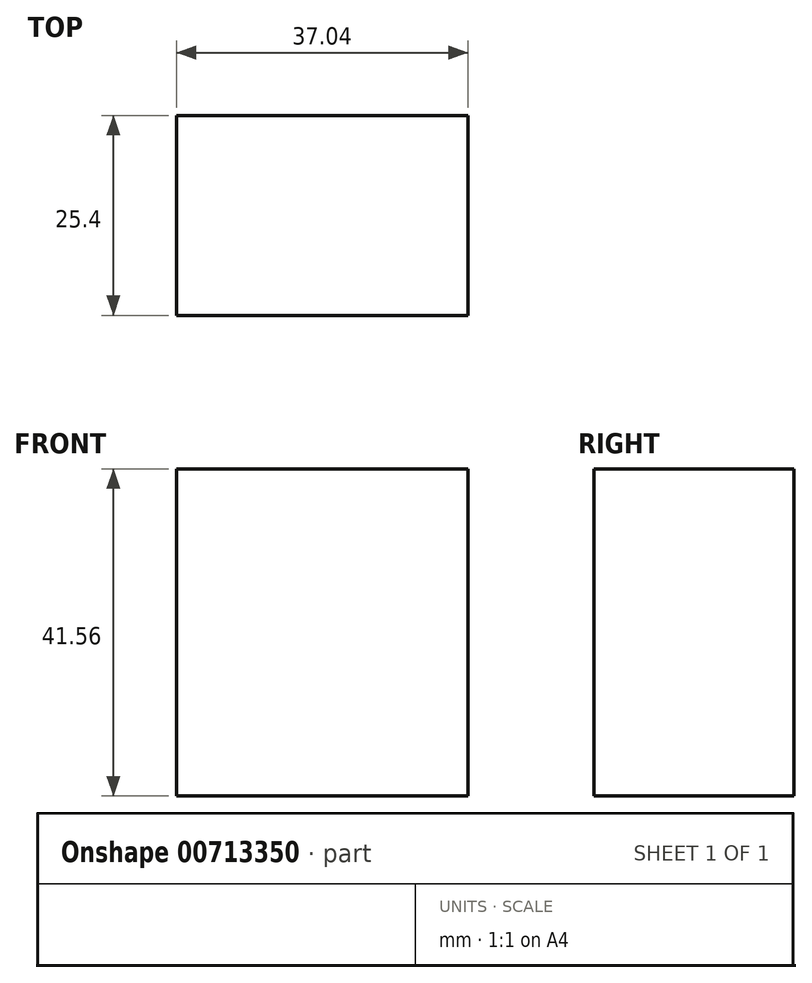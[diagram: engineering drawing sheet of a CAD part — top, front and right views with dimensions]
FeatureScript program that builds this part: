
annotation { "Feature Type Name" : "Feature", "Feature Type Description" : "" }
export const myFeature = defineFeature(function(context is Context, id is Id, definition is map)
    precondition{}
    {
        {
            var Q0;
            Q0=qCreatedBy(makeId("Front.planeOp"),FACE);
            var sketch = newSketch(context, id + "F0", { "sketchPlane" : qUnion([Q0])});
            skLineSegment(sketch, "E0.bottom", {"start": v(0, 0) * mm, "end": v(0, 0) * mm});
            skLineSegment(sketch, "E0.top", {"start": v(0, 0) * mm, "end": v(0, 0) * mm});
            skLineSegment(sketch, "E0.left", {"start": v(0, 0) * mm, "end": v(0, 0) * mm});
            skLineSegment(sketch, "E0.right", {"start": v(0, 0) * mm, "end": v(0, 0) * mm});
            skLineSegment(sketch, "E1.bottom", {"start": v(0, 41.56) * mm, "end": v(37.04, 41.56) * mm});
            skLineSegment(sketch, "E1.top", {"start": v(0, 0) * mm, "end": v(37.04, 0) * mm});
            skLineSegment(sketch, "E1.left", {"start": v(0, 41.56) * mm, "end": v(0, 0) * mm});
            skLineSegment(sketch, "E1.right", {"start": v(37.04, 41.56) * mm, "end": v(37.04, 0) * mm});
            skSolve(sketch);
        }
        {
            var Q0;
            Q0 = qSketchRegion(id + "F0", true);
            extrude(context, id + "F1", {"entities" : qUnion([Q0]), "oppositeDirection" : true, "depth" : 25.4 * mm, "offsetDistance" : 25.4 * mm});
        }
    });
